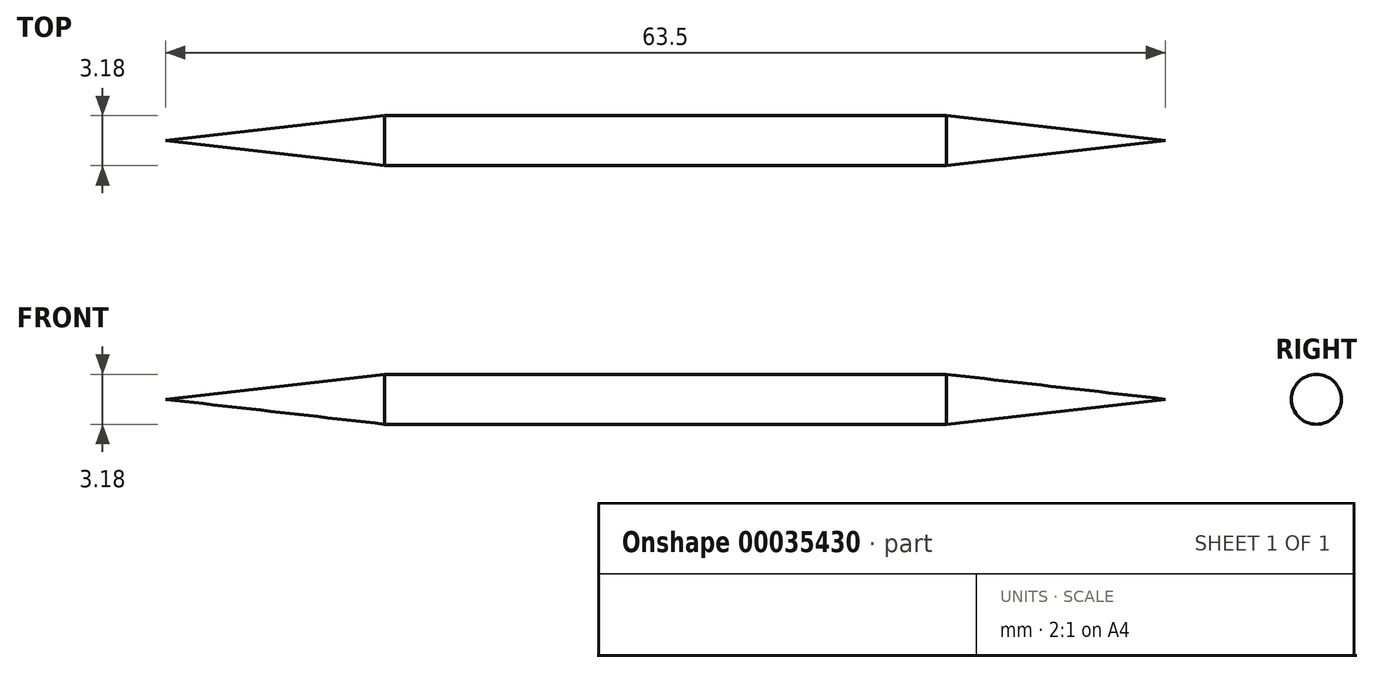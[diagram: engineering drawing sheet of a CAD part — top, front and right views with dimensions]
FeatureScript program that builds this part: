
annotation { "Feature Type Name" : "Feature", "Feature Type Description" : "" }
export const myFeature = defineFeature(function(context is Context, id is Id, definition is map)
    precondition{}
    {
        {
            var Q0;
            Q0=qCreatedBy(makeId("Top.planeOp"),FACE);
            var sketch = newSketch(context, id + "F0", { "sketchPlane" : qUnion([Q0])});
            skLineSegment(sketch, "E0", {"start": v(0, 0) * mm, "end": v(63.5, 0) * mm});
            skLineSegment(sketch, "E1", {"start": v(13.92, 1.59) * mm, "end": v(31.75, 1.59) * mm});
            skLineSegment(sketch, "E2", {"start": v(49.6, 1.59) * mm, "end": v(31.75, 1.59) * mm});
            skPoint(sketch, "E3.start.orphan", {"position": v(31.75, 0) * mm});
            skLineSegment(sketch, "E4", {"start": v(0, 0) * mm, "end": v(13.92, 1.59) * mm});
            skLineSegment(sketch, "E5", {"start": v(63.5, 0) * mm, "end": v(49.6, 1.59) * mm});
            skPoint(sketch, "E6.orphan", {"position": v(44.65, 1.59) * mm});
            skPoint(sketch, "E7.orphan", {"position": v(6.15, 1.59) * mm});
            skLineSegment(sketch, "E8", {"start": v(31.75, 1.59) * mm, "end": v(31.75, 0) * mm});
            skSolve(sketch);
        }
        {
            var Q0;
            Q0=makeQuery(id+"F0.imprint","IMPRINT",FACE,{"disambiguationData":[TD([[makeQuery(id+"F0.imprint","IMPRINT",EDGE,{"derivedFrom":sQuery(id+"F0.wireOp",EDGE,"E0")}),1.0]])]});
            var Q1;
            Q1=sQuery(id+"F0.wireOp",EDGE,"E0");
            revolve(context, id + "F1", {"entities" : qUnion([Q0]), "axis" : qUnion([Q1]), "revolveType" : RevolveType.FULL});
        }
    });
